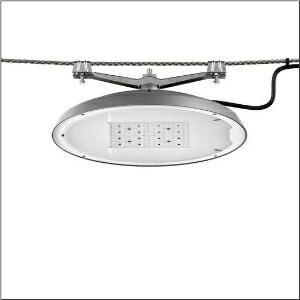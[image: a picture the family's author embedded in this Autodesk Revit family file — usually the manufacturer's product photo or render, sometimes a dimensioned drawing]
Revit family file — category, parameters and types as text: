
# Revit family: dl_r__50_iq_mini___st0_8s_5xa248v41f08me_8e0e
name_source: partatom
category: Lighting Fixtures
units: mm (PartAtom-declared; Revit-internal decimal feet)

## family parameters
Cut with Voids When Loaded = No
Host = Face
Light Source = No
Part Type = Normal
Room Calculation Point = No
Round Connector Dimension = Use Diameter
Shared = No

## types (1)
- --- (1 x LED, 15660 lm, 101.7 W, 4000K)
    Apparent Load = 102 VA
    CIE Flux Codes = 38 75 97 100 100
    Color Rendering = 70
    Color Temperature = 4000K
    Default Elevation = 1800 mm
    Description = DL® 50 iQ mini, catenary luminaire, primary light control with lens, of PMMA, primary optical cover: cover, of toughened safety glass, transparent, light distribution: ST0.8s, light emission: direct distribution, primary light characteristic: symmetric, installation type: suspended mounting, LED, High Power LED, rated luminous flux: 15.660lm, luminous efficacy: 154lm/W, light colour: 740, colour temperature: 4000K, control gear: iQ Street-Remote, control: optimised constant luminous flux control (CLO 2.0), Desk-Remote (wireless, voltage-free reading and setting of iQ features in the workshop via application-optimized NFC function/RFID function), Light-Fading, Smart-Wire, Night-Set, Lumen-Switch, Temp-Guard, Auto-Match, Street-Remote, mains connection: 230..240V, AC, 50/60Hz, start of lifetime: 102W, end of service life: 111W, reduction: 45W, luminaire housing, of diecast aluminium, powder-coated, Siteco® metallic grey (DB 702S), diameter: 500mm, height: 115mm, mounting height: 4..12m, protection rating (complete): IP66, insulation class (complete): insulation class II (safety insulation), certification: CE, ENEC, ENEC+, VDE, impact resistance: IK08, permissible operating ambient temperature for outdoor applications: -25..+40°C, standard-compliant lighting for roads and squares, packaging unit: 1 piece

Light Distribution: ST0.8s
    Height = 124 mm  [stored 0.406824 ft]
    Lamp = 1 x LED
    Lamp Light Flux = 15660 lm
    Lamp Power = 101.7 W
    Lamp count = 1
    Length = 500 mm
    Luminous efficacy = 154 lm/W
    Manufacturer = Siteco
    ModVariant = No
    Model = 5XA248V41F08ME
    Number of Poles = 1
    OnlyDefault = Yes
    Power Factor = 1
    Product Name = DL® 50 iQ mini | ST0.8s
    Product group = catenary luminaire
    ProductGroupID = 6300
    Protection Class = Protection class II
    Protection Degree = IP 66
    RLX_Detail_Level = 1
    RLX_Emergency_Light_Flux = 0 lm
    RLX_Emergency_Type = 0
    RLX_Emergency_Type_DB = No
    RlxData = <blob elided: 127393 chars, md5=910b421e>
    Socket = socket
    Standby Power = 0 W
    System Light Flux = 15660 lm
    System Power = 102 W
    Type Comments = factory setting: luminous flux: 100 % | dim-lin: 254 | 534 mA
    Type Image = l_1251783.jpg
    URL = http://relux.com
    VarID = @adj_140944
    Voltage = 0 V
    Weight = 0.00 kg
    Width = 0 mm  [stored 0 ft]

note: [stored X ft] marks values corroborated as IEEE doubles in the binary element streams (Revit-internal decimal feet)

## geometry (parser evidence)
native form markers: Blend x4, Sweep x16
no freeform markers — native parametric forms only
